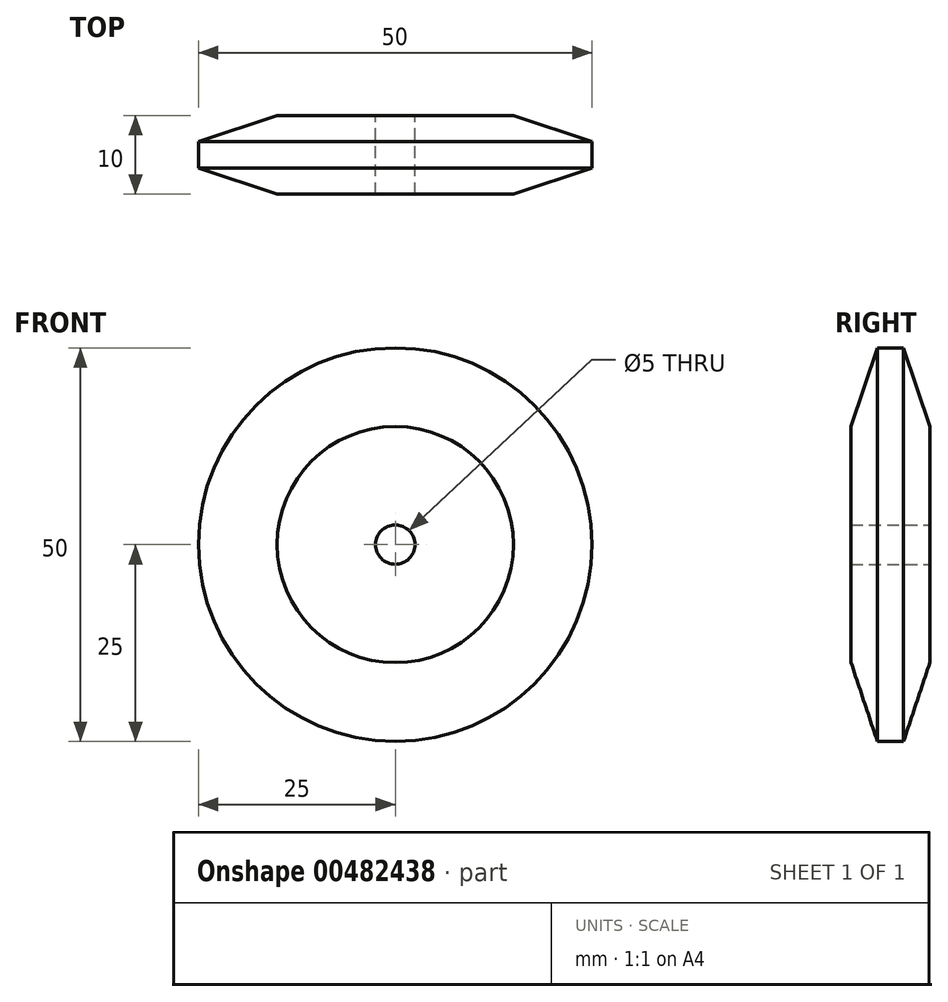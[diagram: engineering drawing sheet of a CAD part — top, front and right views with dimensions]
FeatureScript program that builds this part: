
annotation { "Feature Type Name" : "Feature", "Feature Type Description" : "" }
export const myFeature = defineFeature(function(context is Context, id is Id, definition is map)
    precondition{}
    {
        {
            assignVariable(context, id + "F0", {"name" : "prumer_kola", "anyValue" : 50 * mm});
        }
        {
            assignVariable(context, id + "F1", {"name" : "sirka_kola", "anyValue" : 10 * mm});
        }
        {
            var Q0;
            Q0=qCreatedBy(makeId("Top.planeOp"),FACE);
            var sketch = newSketch(context, id + "F2", { "sketchPlane" : qUnion([Q0])});
            skPoint(sketch, "E0.middle", {"position": v(0, 0) * mm});
            skLineSegment(sketch, "E1", {"start": v(0, 11.44) * mm, "end": v(0, -10.07) * mm, "construction": true});
            skLineSegment(sketch, "E2", {"start": v(0, 0) * mm, "end": v(26.06, 0) * mm, "construction": true});
            skLineSegment(sketch, "E3.bottom", {"start": v(25, 5) * mm, "end": v(2.5, 5) * mm});
            skLineSegment(sketch, "E3.top", {"start": v(25, -5) * mm, "end": v(2.5, -5) * mm});
            skLineSegment(sketch, "E3.left", {"start": v(25, 5) * mm, "end": v(25, -5) * mm});
            skLineSegment(sketch, "E3.right", {"start": v(2.5, 5) * mm, "end": v(2.5, -5) * mm});
            skPoint(sketch, "E3.middle", {"position": v(13.75, 0) * mm});
            skSolve(sketch);
        }
        {
            var Q0;
            Q0=makeQuery(id+"F2.imprint","IMPRINT",FACE,{"disambiguationData":[TD([[makeQuery(id+"F2.imprint","IMPRINT",EDGE,{"derivedFrom":sQuery(id+"F2.wireOp",EDGE,"E3.bottom")}),1.0]])]});
            var Q1;
            Q1=sQuery(id+"F2.wireOp",EDGE,"E1");
            revolve(context, id + "F3", {"entities" : qUnion([Q0]), "axis" : qUnion([Q1]), "revolveType" : RevolveType.FULL});
        }
        {
            var Q0;
            Q0=makeQuery(id+"F3.opRevolve","SWEPT_EDGE",EDGE,{"disambiguationData":[OSD([sQuery(id+"F2.wireOp",EDGE,"E3.bottom"),sQuery(id+"F2.wireOp",EDGE,"E3.left")])]});
            var Q1;
            Q1=makeQuery(id+"F3.opRevolve","SWEPT_EDGE",EDGE,{"disambiguationData":[OSD([sQuery(id+"F2.wireOp",EDGE,"E3.top"),sQuery(id+"F2.wireOp",EDGE,"E3.left")])]});
            chamfer(context, id + "F4", {"entities" : qUnion([Q0, Q1]), "chamferType" : ChamferType.TWO_OFFSETS, "width1" : getVariable(context, 'prumer_kola') / 5, "oppositeDirection" : false, "width2" : getVariable(context, 'sirka_kola') / 3, "tangentPropagation" : true});
        }
    });
